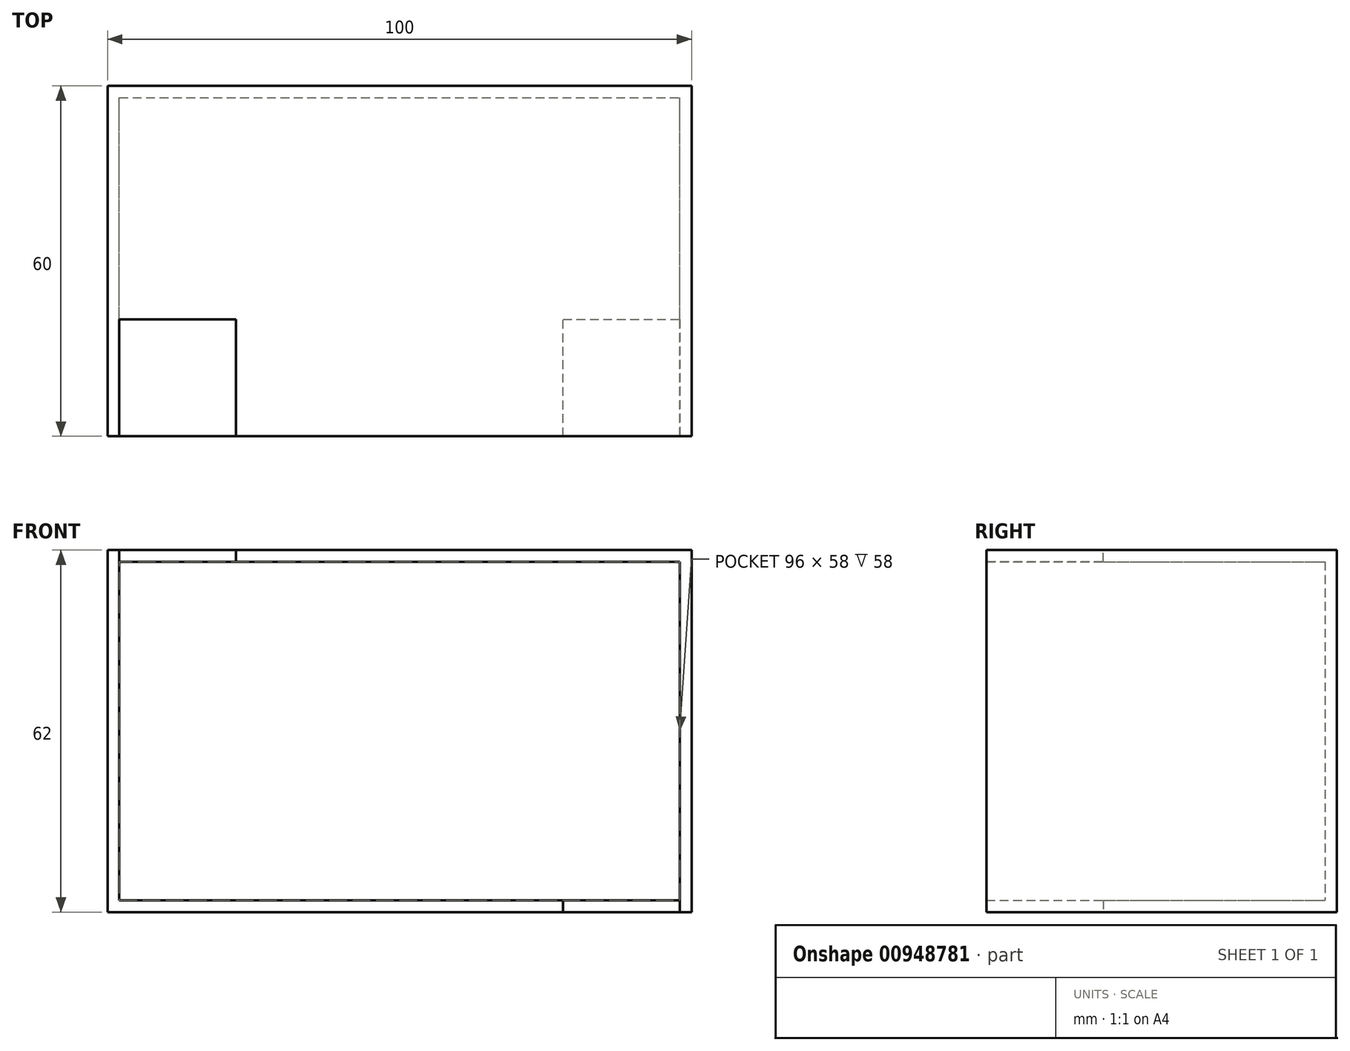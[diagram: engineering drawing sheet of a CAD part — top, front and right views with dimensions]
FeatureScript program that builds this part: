
annotation { "Feature Type Name" : "Feature", "Feature Type Description" : "" }
export const myFeature = defineFeature(function(context is Context, id is Id, definition is map)
    precondition{}
    {
        {
            var Q0;
            Q0=qCreatedBy(makeId("Front.planeOp"),FACE);
            var sketch = newSketch(context, id + "F0", { "sketchPlane" : qUnion([Q0])});
            skLineSegment(sketch, "E0.bottom", {"start": v(-56.37, 30.11) * mm, "end": v(43.63, 30.11) * mm});
            skLineSegment(sketch, "E0.top", {"start": v(-56.37, -31.89) * mm, "end": v(43.63, -31.89) * mm});
            skLineSegment(sketch, "E0.left", {"start": v(-56.37, 30.11) * mm, "end": v(-56.37, -31.89) * mm});
            skLineSegment(sketch, "E0.right", {"start": v(43.63, 30.11) * mm, "end": v(43.63, -31.89) * mm});
            skSolve(sketch);
        }
        {
            var Q0;
            Q0=makeQuery(id+"F0.imprint","IMPRINT",FACE,{"disambiguationData":[TD([[makeQuery(id+"F0.imprint","IMPRINT",EDGE,{"derivedFrom":sQuery(id+"F0.wireOp",EDGE,"E0.bottom")}),-1.0]])]});
            extrude(context, id + "F1", {"entities" : qUnion([Q0]), "depth" : 60 * mm, "offsetDistance" : 25 * mm});
        }
        {
            var Q0;
            Q0=makeQuery(id+"F1.opExtrude","CAP_FACE",FACE,{"disambiguationData":[OSD([sQuery(id+"F0.wireOp",EDGE,"E0.bottom"),sQuery(id+"F0.wireOp",EDGE,"E0.top"),sQuery(id+"F0.wireOp",EDGE,"E0.left"),sQuery(id+"F0.wireOp",EDGE,"E0.right")])],"isStart":false});
            shell(context, id + "F2", {"entities" : qUnion([Q0]), "thickness" : 2 * mm});
        }
        {
            var Q0;
            Q0=makeQuery(id+"F1.opExtrude","SWEPT_FACE",FACE,{"disambiguationData":[OSD([sQuery(id+"F0.wireOp",EDGE,"E0.top")])]});
            var sketch = newSketch(context, id + "F3", { "sketchPlane" : qUnion([Q0])});
            skLineSegment(sketch, "E1.bottom", {"start": v(21.63, 60) * mm, "end": v(41.63, 60) * mm});
            skLineSegment(sketch, "E1.top", {"start": v(21.63, 40) * mm, "end": v(41.63, 40) * mm});
            skLineSegment(sketch, "E1.left", {"start": v(21.63, 60) * mm, "end": v(21.63, 40) * mm});
            skLineSegment(sketch, "E1.right", {"start": v(41.63, 60) * mm, "end": v(41.63, 40) * mm});
            skSolve(sketch);
        }
        {
            var Q0;
            Q0=makeQuery(id+"F3.imprint","IMPRINT",FACE,{"disambiguationData":[TD([[makeQuery(id+"F3.imprint","IMPRINT",EDGE,{"derivedFrom":sQuery(id+"F3.wireOp",EDGE,"E1.bottom")}),-1.0]])]});
            extrude(context, id + "F4", {"entities" : qUnion([Q0]), "operationType" : NewBodyOperationType.REMOVE, "oppositeDirection" : true, "depth" : 2 * mm, "offsetDistance" : 25 * mm});
        }
        {
            var Q0;
            Q0=makeQuery(id+"F1.opExtrude","SWEPT_FACE",FACE,{"disambiguationData":[OSD([sQuery(id+"F0.wireOp",EDGE,"E0.bottom")])]});
            var sketch = newSketch(context, id + "F5", { "sketchPlane" : qUnion([Q0])});
            skLineSegment(sketch, "E2.bottom", {"start": v(-54.37, -40) * mm, "end": v(-34.37, -40) * mm});
            skLineSegment(sketch, "E2.top", {"start": v(-54.37, -60) * mm, "end": v(-34.37, -60) * mm});
            skLineSegment(sketch, "E2.left", {"start": v(-54.37, -40) * mm, "end": v(-54.37, -60) * mm});
            skLineSegment(sketch, "E2.right", {"start": v(-34.37, -40) * mm, "end": v(-34.37, -60) * mm});
            skSolve(sketch);
        }
        {
            var Q0;
            Q0=makeQuery(id+"F5.imprint","IMPRINT",FACE,{"disambiguationData":[TD([[makeQuery(id+"F5.imprint","IMPRINT",EDGE,{"derivedFrom":sQuery(id+"F5.wireOp",EDGE,"E2.bottom")}),-1.0]])]});
            var Q1;
            Q1=sQuery(id+"F5.wireOp",EDGE,"E2.left");
            var Q2;
            Q2=sQuery(id+"F5.wireOp",EDGE,"E2.bottom");
            var Q3;
            Q3=sQuery(id+"F5.wireOp",EDGE,"E2.right");
            var Q4;
            Q4=sQuery(id+"F5.wireOp",EDGE,"E2.top");
            extrude(context, id + "F6", {"entities" : qUnion([Q0]), "operationType" : NewBodyOperationType.REMOVE, "surfaceEntities" : qUnion([Q1, Q2, Q3, Q4]), "oppositeDirection" : true, "depth" : 2 * mm, "offsetDistance" : 25 * mm});
        }
    });
